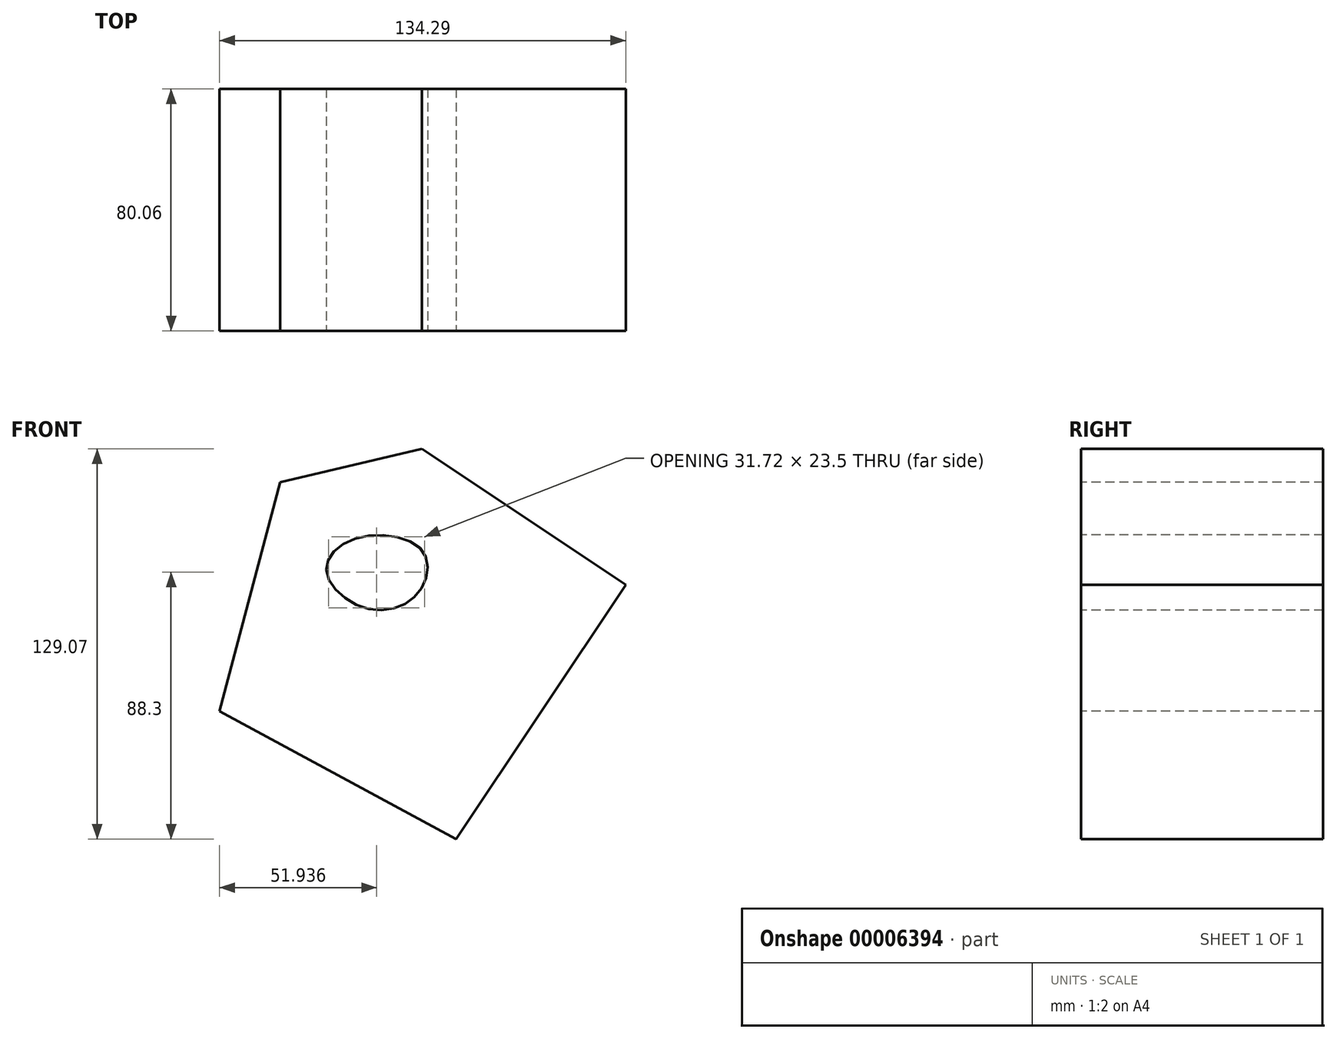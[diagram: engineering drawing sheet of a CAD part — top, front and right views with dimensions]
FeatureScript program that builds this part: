
annotation { "Feature Type Name" : "Feature", "Feature Type Description" : "" }
export const myFeature = defineFeature(function(context is Context, id is Id, definition is map)
    precondition{}
    {
        {
            var Q0;
            Q0=qCreatedBy(makeId("Front.planeOp"),FACE);
            var sketch = newSketch(context, id + "F0", { "sketchPlane" : qUnion([Q0])});
            skLineSegment(sketch, "E0", {"start": v(-106.64, 57.12) * mm, "end": v(-126.62, -18.67) * mm});
            skLineSegment(sketch, "E1", {"start": v(-126.62, -18.67) * mm, "end": v(-48.49, -60.96) * mm});
            skLineSegment(sketch, "E2", {"start": v(-48.49, -60.96) * mm, "end": v(7.67, 23.1) * mm});
            skLineSegment(sketch, "E3", {"start": v(7.67, 23.1) * mm, "end": v(-59.71, 68.1) * mm});
            skLineSegment(sketch, "E4", {"start": v(-59.71, 68.1) * mm, "end": v(-106.64, 57.12) * mm});
            skSolve(sketch);
        }
        {
            var Q0;
            Q0=makeQuery(id+"F0.imprint","IMPRINT",FACE,{"disambiguationData":[TD([[makeQuery(id+"F0.imprint","IMPRINT",EDGE,{"derivedFrom":sQuery(id+"F0.wireOp",EDGE,"E0")}),1.0]])]});
            extrude(context, id + "F1", {"entities" : qUnion([Q0]), "oppositeDirection" : true, "depth" : 80.06 * mm});
        }
        {
            var Q0;
            Q0=makeQuery(id+"F1.opExtrude","CAP_FACE",FACE,{"disambiguationData":[OSD([sQuery(id+"F0.wireOp",EDGE,"E0"),sQuery(id+"F0.wireOp",EDGE,"E1"),sQuery(id+"F0.wireOp",EDGE,"E2"),sQuery(id+"F0.wireOp",EDGE,"E3"),sQuery(id+"F0.wireOp",EDGE,"E4")])],"isStart":true});
            var sketch = newSketch(context, id + "F2", { "sketchPlane" : qUnion([Q0])});
            skFitSpline(sketch, "E5", {"points": [v(-81.85, 38.42) * mm, v(-91.29, 27.35) * mm, v(-77.25, 15.18) * mm, v(-60.56, 20.94) * mm, v(-59.85, 34.75) * mm, v(-81.85, 38.42) * mm]});
            skSolve(sketch);
        }
        {
            var Q0;
            Q0 = qSketchRegion(id + "F2", true);
            var Q1;
            Q1=makeQuery(id+"F1.opExtrude","SWEPT_EDGE",EDGE,{"disambiguationData":[OSD([sQuery(id+"F0.wireOp",EDGE,"E0"),sQuery(id+"F0.wireOp",EDGE,"E4")])]});
            sweep(context, id + "F3", {"operationType" : NewBodyOperationType.REMOVE, "profiles" : qUnion([Q0]), "path" : qUnion([Q1])});
        }
    });
